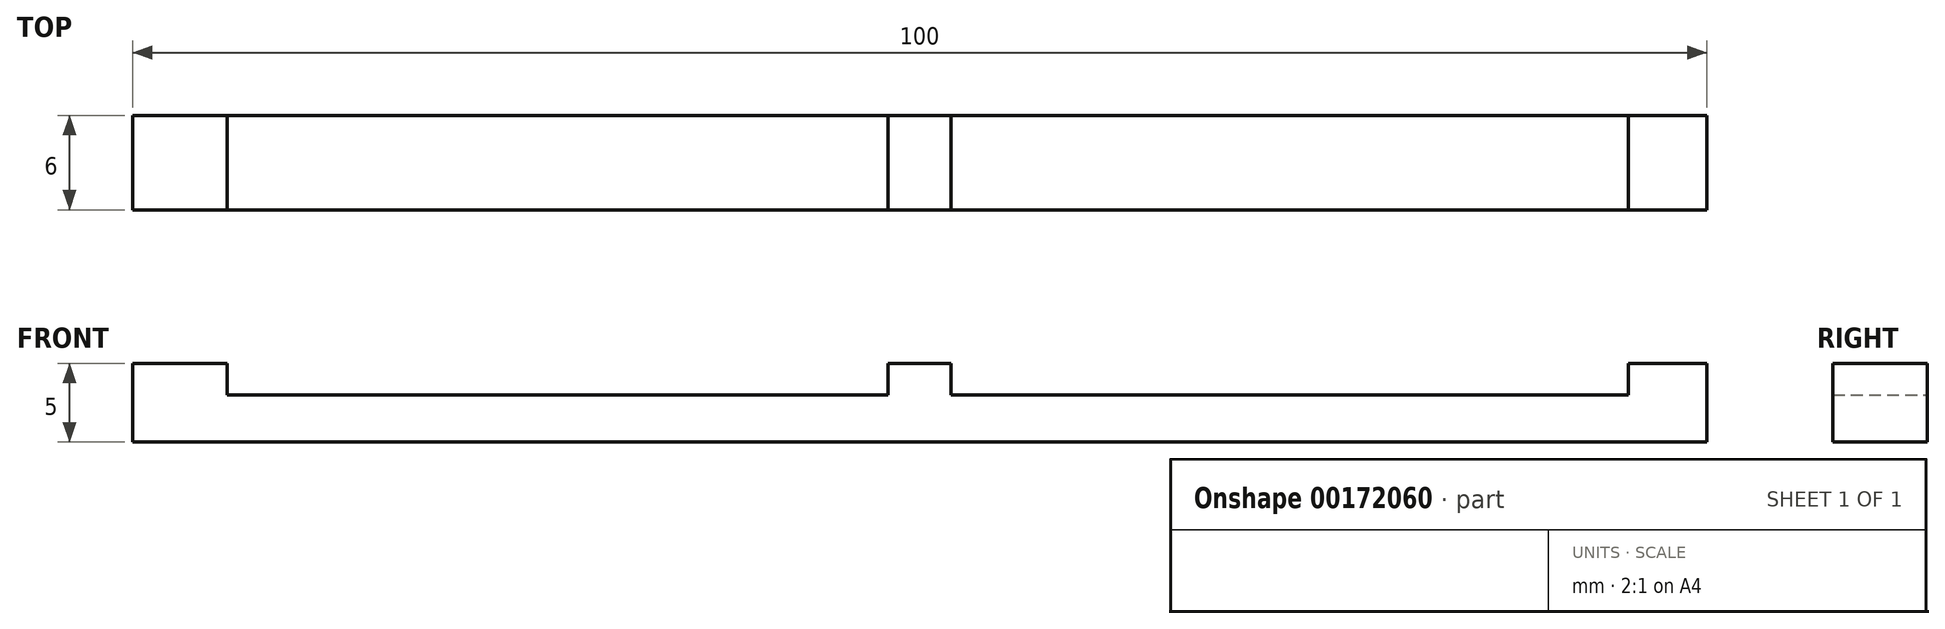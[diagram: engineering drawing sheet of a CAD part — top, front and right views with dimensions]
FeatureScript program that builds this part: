
annotation { "Feature Type Name" : "Feature", "Feature Type Description" : "" }
export const myFeature = defineFeature(function(context is Context, id is Id, definition is map)
    precondition{}
    {
        {
            var Q0;
            Q0=qCreatedBy(makeId("Top.planeOp"),FACE);
            var sketch = newSketch(context, id + "F0", { "sketchPlane" : qUnion([Q0])});
            skLineSegment(sketch, "E0.bottom", {"start": v(50, -3) * mm, "end": v(-50, -3) * mm});
            skLineSegment(sketch, "E0.top", {"start": v(50, 3) * mm, "end": v(-50, 3) * mm});
            skLineSegment(sketch, "E0.left", {"start": v(50, -3) * mm, "end": v(50, 3) * mm});
            skLineSegment(sketch, "E0.right", {"start": v(-50, -3) * mm, "end": v(-50, 3) * mm});
            skPoint(sketch, "E0.middle", {"position": v(0, 0) * mm});
            skSolve(sketch);
        }
        {
            var Q0;
            Q0 = qSketchRegion(id + "F0", true);
            extrude(context, id + "F1", {"entities" : qUnion([Q0]), "depth" : 3 * mm});
        }
        {
            var Q0;
            Q0=makeQuery(id+"F1.opExtrude","CAP_FACE",FACE,{"disambiguationData":[OSD([sQuery(id+"F0.wireOp",EDGE,"E0.bottom"),sQuery(id+"F0.wireOp",EDGE,"E0.top"),sQuery(id+"F0.wireOp",EDGE,"E0.left"),sQuery(id+"F0.wireOp",EDGE,"E0.right")])],"isStart":false});
            var sketch = newSketch(context, id + "F2", { "sketchPlane" : qUnion([Q0])});
            skLineSegment(sketch, "E1.bottom", {"start": v(-50, 3) * mm, "end": v(-44, 3) * mm});
            skLineSegment(sketch, "E1.top", {"start": v(-50, -3) * mm, "end": v(-44, -3) * mm});
            skLineSegment(sketch, "E1.left", {"start": v(-50, 3) * mm, "end": v(-50, -3) * mm});
            skLineSegment(sketch, "E1.right", {"start": v(-44, 3) * mm, "end": v(-44, -3) * mm});
            skLineSegment(sketch, "E2.bottom", {"start": v(2, -3) * mm, "end": v(-2, -3) * mm});
            skLineSegment(sketch, "E2.top", {"start": v(2, 3) * mm, "end": v(-2, 3) * mm});
            skLineSegment(sketch, "E2.left", {"start": v(2, -3) * mm, "end": v(2, 3) * mm});
            skLineSegment(sketch, "E2.right", {"start": v(-2, -3) * mm, "end": v(-2, 3) * mm});
            skPoint(sketch, "E2.middle", {"position": v(0, 0) * mm});
            skLineSegment(sketch, "E3.bottom", {"start": v(50, 3) * mm, "end": v(45, 3) * mm});
            skLineSegment(sketch, "E3.top", {"start": v(50, -3) * mm, "end": v(45, -3) * mm});
            skLineSegment(sketch, "E3.left", {"start": v(50, 3) * mm, "end": v(50, -3) * mm});
            skLineSegment(sketch, "E3.right", {"start": v(45, 3) * mm, "end": v(45, -3) * mm});
            skSolve(sketch);
        }
        {
            var Q0;
            Q0 = qSketchRegion(id + "F2", true);
            extrude(context, id + "F3", {"entities" : qUnion([Q0]), "operationType" : NewBodyOperationType.ADD, "depth" : 2 * mm});
        }
    });
